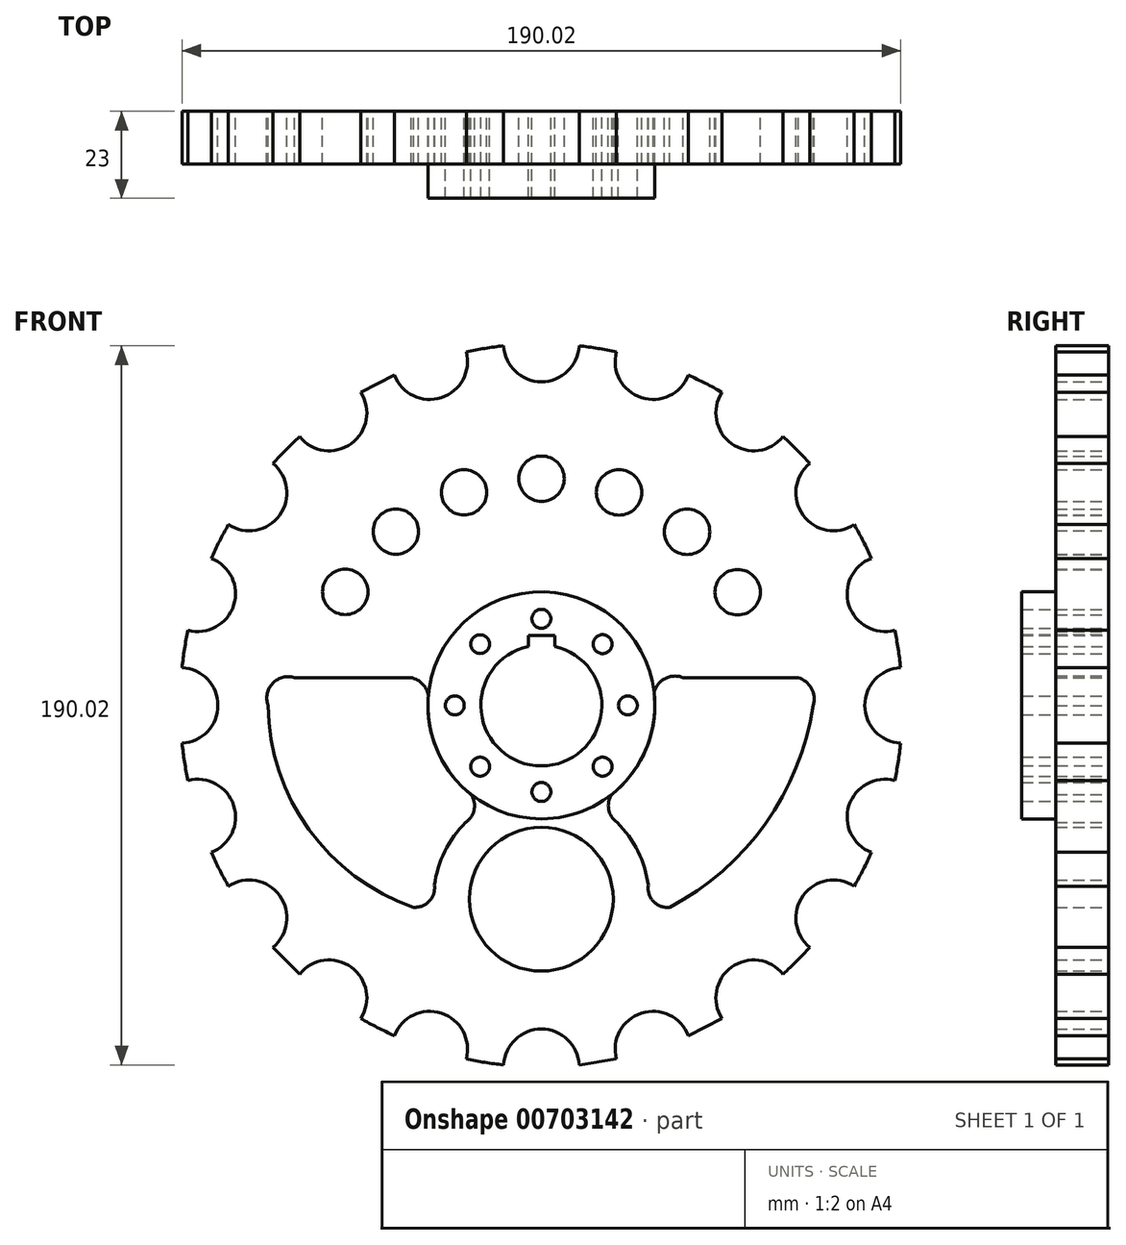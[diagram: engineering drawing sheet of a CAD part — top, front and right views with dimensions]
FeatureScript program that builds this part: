
annotation { "Feature Type Name" : "Feature", "Feature Type Description" : "" }
export const myFeature = defineFeature(function(context is Context, id is Id, definition is map)
    precondition{}
    {
        {
            var Q0;
            Q0=qCreatedBy(makeId("Front.planeOp"),FACE);
            var sketch = newSketch(context, id + "F0", { "sketchPlane" : qUnion([Q0])});
            skPoint(sketch, "E0.center", {"position": v(0, 0) * mm});
            skCircle(sketch, "E1", {"center": v(0, 0) * mm, "radius": 16 * mm});
            skCircle(sketch, "E2", {"center": v(0, -51.2) * mm, "radius": 19 * mm});
            skArc(sketch, "E3", {"start": v(-18.75, -29.74) * mm, "mid": v(-0.1, -79.7) * mm, "end": v(18.9, -29.87) * mm});
            skCircle(sketch, "E4", {"center": v(0, 0) * mm, "radius": 80.03 * mm});
            skCircle(sketch, "E5", {"center": v(0, 0) * mm, "radius": 30 * mm});
            skCircle(sketch, "E6", {"center": v(-51.86, 30) * mm, "radius": 6 * mm});
            skLineSegment(sketch, "E7", {"start": v(0, 30) * mm, "end": v(-85.73, 30) * mm});
            skCircle(sketch, "E8.1.0", {"center": v(-38.47, 45.93) * mm, "radius": 6 * mm});
            skCircle(sketch, "E8.2.0", {"center": v(-20.44, 56.31) * mm, "radius": 6 * mm});
            skCircle(sketch, "E8.3.0", {"center": v(0.05, 59.9) * mm, "radius": 6 * mm});
            skCircle(sketch, "E8.4.0", {"center": v(20.54, 56.28) * mm, "radius": 6 * mm});
            skCircle(sketch, "E8.5.0", {"center": v(38.55, 45.86) * mm, "radius": 6 * mm});
            skCircle(sketch, "E8.6.0", {"center": v(51.9, 29.9) * mm, "radius": 6 * mm});
            skLineSegment(sketch, "E8.anchor1", {"start": v(0, 0) * mm, "end": v(-51.86, 30) * mm, "construction": true});
            skLineSegment(sketch, "E8.anchor2", {"start": v(0, 0) * mm, "end": v(51.9, 29.9) * mm, "construction": true});
            skCircle(sketch, "E9", {"center": v(0, 22.89) * mm, "radius": 2.5 * mm});
            skCircle(sketch, "E10.1.0", {"center": v(-16.18, 16.18) * mm, "radius": 2.5 * mm});
            skCircle(sketch, "E10.2.0", {"center": v(-22.89, 0) * mm, "radius": 2.5 * mm});
            skCircle(sketch, "E10.3.0", {"center": v(-16.18, -16.18) * mm, "radius": 2.5 * mm});
            skCircle(sketch, "E10.4.0", {"center": v(0, -22.89) * mm, "radius": 2.5 * mm});
            skCircle(sketch, "E10.5.0", {"center": v(16.18, -16.18) * mm, "radius": 2.5 * mm});
            skCircle(sketch, "E10.6.0", {"center": v(22.89, 0) * mm, "radius": 2.5 * mm});
            skCircle(sketch, "E10.7.0", {"center": v(16.18, 16.18) * mm, "radius": 2.5 * mm});
            skArc(sketch, "E11", {"start": v(-20.02, -30.92) * mm, "mid": v(-17.75, -27.52) * mm, "end": v(-18.61, -23.53) * mm});
            skArc(sketch, "E12", {"start": v(18.61, -23.53) * mm, "mid": v(17.8, -27.5) * mm, "end": v(20.02, -30.92) * mm});
            skArc(sketch, "E13", {"start": v(-65.22, 7.36) * mm, "mid": v(-71.02, 5.86) * mm, "end": v(-72.28, 0) * mm});
            skArc(sketch, "E14", {"start": v(-33.75, -53.35) * mm, "mid": v(-29.65, -51.77) * mm, "end": v(-28.27, -47.6) * mm});
            skArc(sketch, "E15", {"start": v(-30, 0) * mm, "mid": v(-30.65, 4.63) * mm, "end": v(-34.44, 7.36) * mm});
            skLineSegment(sketch, "E16", {"start": v(-65.22, 7.36) * mm, "end": v(-34.44, 7.36) * mm});
            skArc(sketch, "E17", {"start": v(-72.28, 0) * mm, "mid": v(-61.48, -32.78) * mm, "end": v(-33.75, -53.35) * mm});
            skPoint(sketch, "E18.startSnap0", {"position": v(-49.83, 7.36) * mm});
            skArc(sketch, "E19", {"start": v(37.43, 7.36) * mm, "mid": v(31.33, 6.1) * mm, "end": v(30, 0) * mm});
            skArc(sketch, "E20", {"start": v(28.27, -47.6) * mm, "mid": v(29.67, -51.86) * mm, "end": v(33.9, -53.35) * mm});
            skPoint(sketch, "E21", {"position": v(71.9, 7.36) * mm});
            skArc(sketch, "E22", {"start": v(71.9, 0) * mm, "mid": v(71.41, 4.48) * mm, "end": v(67.94, 7.36) * mm});
            skArc(sketch, "E23", {"start": v(33.9, -53.35) * mm, "mid": v(59.27, -31.2) * mm, "end": v(71.9, 0) * mm});
            skLineSegment(sketch, "E24", {"start": v(37.43, 7.36) * mm, "end": v(67.94, 7.36) * mm});
            skArc(sketch, "E25", {"start": v(-9.99, 95) * mm, "mid": v(0, 85.53) * mm, "end": v(9.99, 95) * mm});
            skArc(sketch, "E26.1.0", {"start": v(-38.86, 87.27) * mm, "mid": v(-26.43, 81.35) * mm, "end": v(-19.86, 93.45) * mm});
            skArc(sketch, "E26.2.0", {"start": v(-63.92, 71) * mm, "mid": v(-50.27, 69.2) * mm, "end": v(-47.77, 82.73) * mm});
            skArc(sketch, "E26.3.0", {"start": v(-82.73, 47.77) * mm, "mid": v(-69.2, 50.27) * mm, "end": v(-71, 63.92) * mm});
            skArc(sketch, "E26.4.0", {"start": v(-93.45, 19.86) * mm, "mid": v(-81.35, 26.43) * mm, "end": v(-87.27, 38.86) * mm});
            skArc(sketch, "E26.5.0", {"start": v(-95, -9.99) * mm, "mid": v(-85.53, 0) * mm, "end": v(-95, 9.99) * mm});
            skArc(sketch, "E26.6.0", {"start": v(-87.27, -38.86) * mm, "mid": v(-81.35, -26.43) * mm, "end": v(-93.45, -19.86) * mm});
            skArc(sketch, "E26.7.0", {"start": v(-71, -63.92) * mm, "mid": v(-69.2, -50.27) * mm, "end": v(-82.73, -47.77) * mm});
            skArc(sketch, "E26.8.0", {"start": v(-47.77, -82.73) * mm, "mid": v(-50.27, -69.2) * mm, "end": v(-63.92, -71) * mm});
            skArc(sketch, "E26.9.0", {"start": v(-19.86, -93.45) * mm, "mid": v(-26.43, -81.35) * mm, "end": v(-38.86, -87.27) * mm});
            skArc(sketch, "E26.10.0", {"start": v(9.99, -95) * mm, "mid": v(0, -85.53) * mm, "end": v(-9.99, -95) * mm});
            skArc(sketch, "E26.11.0", {"start": v(38.86, -87.27) * mm, "mid": v(26.43, -81.35) * mm, "end": v(19.86, -93.45) * mm});
            skArc(sketch, "E26.12.0", {"start": v(63.92, -71) * mm, "mid": v(50.27, -69.2) * mm, "end": v(47.77, -82.73) * mm});
            skArc(sketch, "E26.13.0", {"start": v(82.73, -47.77) * mm, "mid": v(69.2, -50.27) * mm, "end": v(71, -63.92) * mm});
            skArc(sketch, "E26.14.0", {"start": v(93.45, -19.86) * mm, "mid": v(81.35, -26.43) * mm, "end": v(87.27, -38.86) * mm});
            skArc(sketch, "E26.15.0", {"start": v(95, 9.99) * mm, "mid": v(85.53, 0) * mm, "end": v(95, -9.99) * mm});
            skArc(sketch, "E26.16.0", {"start": v(87.27, 38.86) * mm, "mid": v(81.35, 26.43) * mm, "end": v(93.45, 19.86) * mm});
            skArc(sketch, "E26.17.0", {"start": v(71, 63.92) * mm, "mid": v(69.2, 50.27) * mm, "end": v(82.73, 47.77) * mm});
            skArc(sketch, "E26.18.0", {"start": v(47.77, 82.73) * mm, "mid": v(50.27, 69.2) * mm, "end": v(63.92, 71) * mm});
            skArc(sketch, "E26.19.0", {"start": v(19.86, 93.45) * mm, "mid": v(26.43, 81.35) * mm, "end": v(38.86, 87.27) * mm});
            skArc(sketch, "E27", {"start": v(-63.92, 71) * mm, "mid": v(-67.55, 67.55) * mm, "end": v(-71, 63.92) * mm});
            skArc(sketch, "E28.trimOffspring", {"start": v(-9.99, 95) * mm, "mid": v(-14.94, 94.36) * mm, "end": v(-19.86, 93.45) * mm});
            skArc(sketch, "E29.trimOffspring", {"start": v(19.86, 93.45) * mm, "mid": v(14.94, 94.36) * mm, "end": v(9.99, 95) * mm});
            skArc(sketch, "E30.trimOffspring", {"start": v(47.77, 82.73) * mm, "mid": v(43.37, 85.12) * mm, "end": v(38.86, 87.27) * mm});
            skArc(sketch, "E31.trimOffspring", {"start": v(71, 63.92) * mm, "mid": v(67.55, 67.55) * mm, "end": v(63.92, 71) * mm});
            skArc(sketch, "E32.trimOffspring", {"start": v(87.27, 38.86) * mm, "mid": v(85.12, 43.37) * mm, "end": v(82.73, 47.77) * mm});
            skArc(sketch, "E33.trimOffspring", {"start": v(95, 9.99) * mm, "mid": v(94.36, 14.94) * mm, "end": v(93.45, 19.86) * mm});
            skArc(sketch, "E34.trimOffspring", {"start": v(93.45, -19.86) * mm, "mid": v(94.36, -14.94) * mm, "end": v(95, -9.99) * mm});
            skArc(sketch, "E35.trimOffspring", {"start": v(82.73, -47.77) * mm, "mid": v(85.12, -43.37) * mm, "end": v(87.27, -38.86) * mm});
            skArc(sketch, "E36.trimOffspring", {"start": v(63.92, -71) * mm, "mid": v(67.55, -67.55) * mm, "end": v(71, -63.92) * mm});
            skArc(sketch, "E37.trimOffspring", {"start": v(-19.86, -93.45) * mm, "mid": v(-14.94, -94.36) * mm, "end": v(-9.99, -95) * mm});
            skArc(sketch, "E38.trimOffspring", {"start": v(-47.77, -82.73) * mm, "mid": v(-43.37, -85.12) * mm, "end": v(-38.86, -87.27) * mm});
            skArc(sketch, "E39.trimOffspring", {"start": v(-87.27, -38.86) * mm, "mid": v(-85.12, -43.37) * mm, "end": v(-82.73, -47.77) * mm});
            skArc(sketch, "E40.trimOffspring", {"start": v(-95, -9.99) * mm, "mid": v(-94.36, -14.94) * mm, "end": v(-93.45, -19.86) * mm});
            skArc(sketch, "E41.trimOffspring", {"start": v(-93.45, 19.86) * mm, "mid": v(-94.36, 14.94) * mm, "end": v(-95, 9.99) * mm});
            skArc(sketch, "E42.trimOffspring", {"start": v(-82.73, 47.77) * mm, "mid": v(-85.12, 43.37) * mm, "end": v(-87.27, 38.86) * mm});
            skLineSegment(sketch, "E43", {"start": v(-47.77, 82.73) * mm, "end": v(-38.86, 87.27) * mm});
            skLineSegment(sketch, "E44", {"start": v(38.86, -87.27) * mm, "end": v(47.77, -82.73) * mm});
            skLineSegment(sketch, "E45", {"start": v(9.99, -95) * mm, "end": v(19.86, -93.45) * mm});
            skLineSegment(sketch, "E46", {"start": v(-71, -63.92) * mm, "end": v(-63.92, -71) * mm});
            skLineSegment(sketch, "E47", {"start": v(-3.47, 15.62) * mm, "end": v(-3.47, 18.47) * mm});
            skLineSegment(sketch, "E48", {"start": v(3.5, 15.61) * mm, "end": v(3.5, 18.47) * mm});
            skLineSegment(sketch, "E49", {"start": v(3.5, 18.47) * mm, "end": v(-3.47, 18.47) * mm});
            skSolve(sketch);
        }
        {
            var Q0;
            Q0 = qSketchRegion(id + "F0", true);
            var Q1;
            Q1=makeQuery(id+"F0.imprint","IMPRINT",FACE,{"disambiguationData":[TD([[makeQuery(id+"F0.imprint","IMPRINT",EDGE,{"derivedFrom":sQuery(id+"F0.wireOp",EDGE,"E4")}),1.0]])]});
            var Q2;
            Q2=makeQuery(id+"F0.imprint","IMPRINT",FACE,{"disambiguationData":[TD([[makeQuery(id+"F0.imprint","IMPRINT",EDGE,{"derivedFrom":sQuery(id+"F0.wireOp",EDGE,"E2")}),-1.0]])]});
            var Q3;
            Q3=makeQuery(id+"F0.imprint","IMPRINT",FACE,{"disambiguationData":[TD([[makeQuery(id+"F0.imprint","IMPRINT",EDGE,{"derivedFrom":sQuery(id+"F0.wireOp",EDGE,"E9")}),-1.0]])]});
            extrude(context, id + "F1", {"entities" : qUnion([Q0, Q1, Q2, Q3]), "depth" : 14 * mm, "offsetDistance" : 25 * mm});
        }
        {
            var Q0;
            Q0=makeQuery(id+"F1.opExtrude","CAP_FACE",FACE,{"disambiguationData":[OSD([sQuery(id+"F0.wireOp",EDGE,"E1"),sQuery(id+"F0.wireOp",EDGE,"E2"),sQuery(id+"F0.wireOp",EDGE,"E3"),sQuery(id+"F0.wireOp",EDGE,"E5"),sQuery(id+"F0.wireOp",EDGE,"E6"),sQuery(id+"F0.wireOp",EDGE,"E8.1.0"),sQuery(id+"F0.wireOp",EDGE,"E8.2.0"),sQuery(id+"F0.wireOp",EDGE,"E8.3.0"),sQuery(id+"F0.wireOp",EDGE,"E8.4.0"),sQuery(id+"F0.wireOp",EDGE,"E8.5.0"),sQuery(id+"F0.wireOp",EDGE,"E8.6.0"),sQuery(id+"F0.wireOp",EDGE,"E9"),sQuery(id+"F0.wireOp",EDGE,"E10.1.0"),sQuery(id+"F0.wireOp",EDGE,"E10.2.0"),sQuery(id+"F0.wireOp",EDGE,"E10.3.0"),sQuery(id+"F0.wireOp",EDGE,"E10.4.0"),sQuery(id+"F0.wireOp",EDGE,"E10.5.0"),sQuery(id+"F0.wireOp",EDGE,"E10.6.0"),sQuery(id+"F0.wireOp",EDGE,"E10.7.0"),sQuery(id+"F0.wireOp",EDGE,"E11"),sQuery(id+"F0.wireOp",EDGE,"E12"),sQuery(id+"F0.wireOp",EDGE,"E13"),sQuery(id+"F0.wireOp",EDGE,"E14"),sQuery(id+"F0.wireOp",EDGE,"E15"),sQuery(id+"F0.wireOp",EDGE,"E16"),sQuery(id+"F0.wireOp",EDGE,"E17"),sQuery(id+"F0.wireOp",EDGE,"E19"),sQuery(id+"F0.wireOp",EDGE,"E20"),sQuery(id+"F0.wireOp",EDGE,"E22"),sQuery(id+"F0.wireOp",EDGE,"E23"),sQuery(id+"F0.wireOp",EDGE,"E24"),sQuery(id+"F0.wireOp",EDGE,"E25"),sQuery(id+"F0.wireOp",EDGE,"E26.1.0"),sQuery(id+"F0.wireOp",EDGE,"E26.2.0"),sQuery(id+"F0.wireOp",EDGE,"E26.3.0"),sQuery(id+"F0.wireOp",EDGE,"E26.4.0"),sQuery(id+"F0.wireOp",EDGE,"E26.5.0"),sQuery(id+"F0.wireOp",EDGE,"E26.6.0"),sQuery(id+"F0.wireOp",EDGE,"E26.7.0"),sQuery(id+"F0.wireOp",EDGE,"E26.8.0"),sQuery(id+"F0.wireOp",EDGE,"E26.9.0"),sQuery(id+"F0.wireOp",EDGE,"E26.10.0"),sQuery(id+"F0.wireOp",EDGE,"E26.11.0"),sQuery(id+"F0.wireOp",EDGE,"E26.12.0"),sQuery(id+"F0.wireOp",EDGE,"E26.13.0"),sQuery(id+"F0.wireOp",EDGE,"E26.14.0"),sQuery(id+"F0.wireOp",EDGE,"E26.15.0"),sQuery(id+"F0.wireOp",EDGE,"E26.16.0"),sQuery(id+"F0.wireOp",EDGE,"E26.17.0"),sQuery(id+"F0.wireOp",EDGE,"E26.18.0"),sQuery(id+"F0.wireOp",EDGE,"E26.19.0"),sQuery(id+"F0.wireOp",EDGE,"E27"),sQuery(id+"F0.wireOp",EDGE,"E28.trimOffspring"),sQuery(id+"F0.wireOp",EDGE,"E29.trimOffspring"),sQuery(id+"F0.wireOp",EDGE,"E30.trimOffspring"),sQuery(id+"F0.wireOp",EDGE,"E31.trimOffspring"),sQuery(id+"F0.wireOp",EDGE,"E32.trimOffspring"),sQuery(id+"F0.wireOp",EDGE,"E33.trimOffspring"),sQuery(id+"F0.wireOp",EDGE,"E34.trimOffspring"),sQuery(id+"F0.wireOp",EDGE,"E35.trimOffspring"),sQuery(id+"F0.wireOp",EDGE,"E36.trimOffspring"),sQuery(id+"F0.wireOp",EDGE,"E37.trimOffspring"),sQuery(id+"F0.wireOp",EDGE,"E38.trimOffspring"),sQuery(id+"F0.wireOp",EDGE,"E39.trimOffspring"),sQuery(id+"F0.wireOp",EDGE,"E40.trimOffspring"),sQuery(id+"F0.wireOp",EDGE,"E41.trimOffspring"),sQuery(id+"F0.wireOp",EDGE,"E42.trimOffspring"),sQuery(id+"F0.wireOp",EDGE,"E43"),sQuery(id+"F0.wireOp",EDGE,"E44"),sQuery(id+"F0.wireOp",EDGE,"E45"),sQuery(id+"F0.wireOp",EDGE,"E46"),sQuery(id+"F0.wireOp",EDGE,"E47"),sQuery(id+"F0.wireOp",EDGE,"E48"),sQuery(id+"F0.wireOp",EDGE,"E49")])],"isStart":false});
            var sketch = newSketch(context, id + "F2", { "sketchPlane" : qUnion([Q0])});
            skCircle(sketch, "E50", {"center": v(0, 0) * mm, "radius": 30 * mm});
            skCircle(sketch, "E51", {"center": v(-16.18, 16.18) * mm, "radius": 2.48 * mm});
            skCircle(sketch, "E52", {"center": v(0, 22.89) * mm, "radius": 2.5 * mm});
            skCircle(sketch, "E53", {"center": v(16.18, 16.18) * mm, "radius": 2.5 * mm});
            skCircle(sketch, "E54", {"center": v(22.89, 0) * mm, "radius": 2.5 * mm});
            skCircle(sketch, "E55", {"center": v(16.18, -16.18) * mm, "radius": 2.5 * mm});
            skCircle(sketch, "E56", {"center": v(0, -22.89) * mm, "radius": 2.5 * mm});
            skCircle(sketch, "E57", {"center": v(-16.18, -16.18) * mm, "radius": 2.5 * mm});
            skCircle(sketch, "E58", {"center": v(-22.89, 0) * mm, "radius": 2.5 * mm});
            skLineSegment(sketch, "E59", {"start": v(-3.47, 15.62) * mm, "end": v(-3.47, 18.47) * mm});
            skLineSegment(sketch, "E60", {"start": v(-3.47, 18.47) * mm, "end": v(3.5, 18.47) * mm});
            skLineSegment(sketch, "E61", {"start": v(3.5, 18.47) * mm, "end": v(3.5, 15.61) * mm});
            skCircle(sketch, "E62", {"center": v(0, 0) * mm, "radius": 16 * mm});
            skSolve(sketch);
        }
        {
            var Q0;
            Q0 = qSketchRegion(id + "F2", true);
            extrude(context, id + "F3", {"entities" : qUnion([Q0]), "operationType" : NewBodyOperationType.ADD, "depth" : 9 * mm, "offsetDistance" : 25 * mm});
        }
    });
